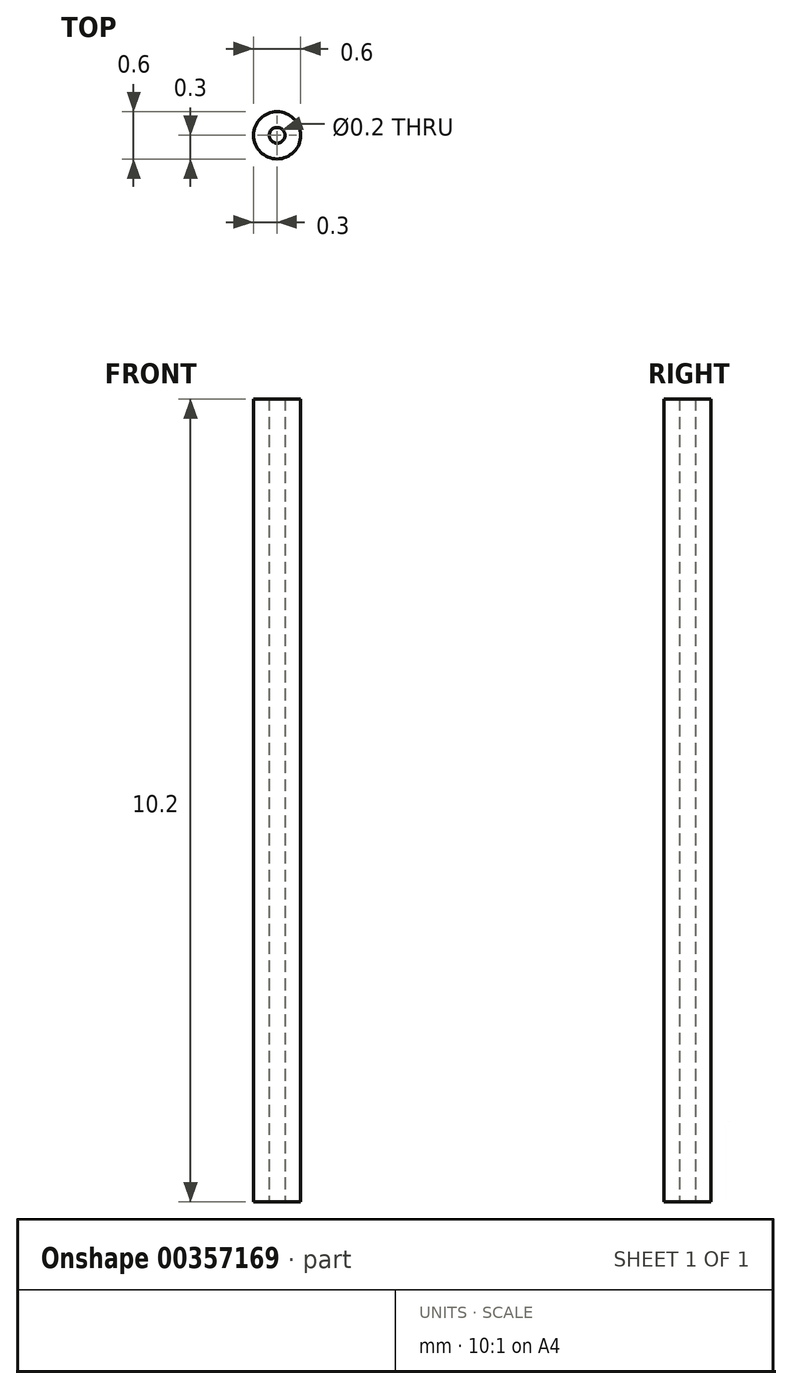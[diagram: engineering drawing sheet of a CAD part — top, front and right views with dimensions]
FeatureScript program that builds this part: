
annotation { "Feature Type Name" : "Feature", "Feature Type Description" : "" }
export const myFeature = defineFeature(function(context is Context, id is Id, definition is map)
    precondition{}
    {
        {
            var Q0;
            Q0=qCreatedBy(makeId("Top.planeOp"),FACE);
            var sketch = newSketch(context, id + "F0", { "sketchPlane" : qUnion([Q0])});
            skCircle(sketch, "E0", {"center": v(0, 0) * mm, "radius": 0.3 * mm});
            skCircle(sketch, "E1", {"center": v(0, 0) * mm, "radius": 0.1 * mm});
            skSolve(sketch);
        }
        {
            var Q0;
            Q0=qSketchRegion(id+"F0",true);
            extrude(context, id + "F1", {"entities" : qUnion([Q0]), "endBound" : BoundingType.SYMMETRIC, "depth" : 10.2 * mm});
        }
    });
